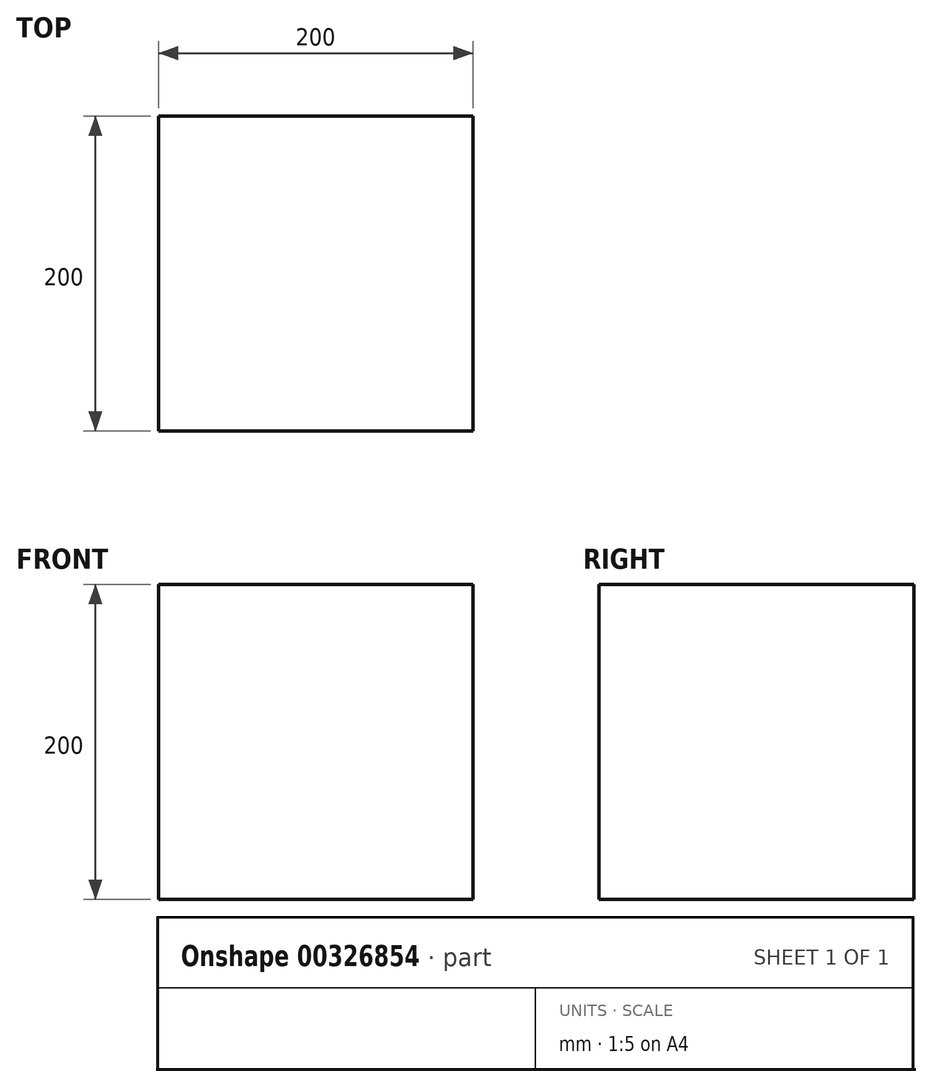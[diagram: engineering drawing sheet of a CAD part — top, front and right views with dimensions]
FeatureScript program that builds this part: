
annotation { "Feature Type Name" : "Feature", "Feature Type Description" : "" }
export const myFeature = defineFeature(function(context is Context, id is Id, definition is map)
    precondition{}
    {
        {
            var Q0;
            Q0=qCreatedBy(makeId("Front.planeOp"),FACE);
            var sketch = newSketch(context, id + "F0", { "sketchPlane" : qUnion([Q0])});
            skLineSegment(sketch, "E0.bottom", {"start": v(-34.21, 178.18) * mm, "end": v(165.79, 178.18) * mm});
            skLineSegment(sketch, "E0.top", {"start": v(-34.21, -21.82) * mm, "end": v(165.79, -21.82) * mm});
            skLineSegment(sketch, "E0.left", {"start": v(-34.21, 178.18) * mm, "end": v(-34.21, -21.82) * mm});
            skLineSegment(sketch, "E0.right", {"start": v(165.79, 178.18) * mm, "end": v(165.79, -21.82) * mm});
            skSolve(sketch);
        }
        {
            var Q0;
            Q0=makeQuery(id+"F0.imprint","IMPRINT",FACE,{"disambiguationData":[TD([[makeQuery(id+"F0.imprint","IMPRINT",EDGE,{"derivedFrom":sQuery(id+"F0.wireOp",EDGE,"E0.bottom")}),-1.0]])]});
            extrude(context, id + "F1", {"entities" : qUnion([Q0]), "depth" : 200 * mm});
        }
    });
